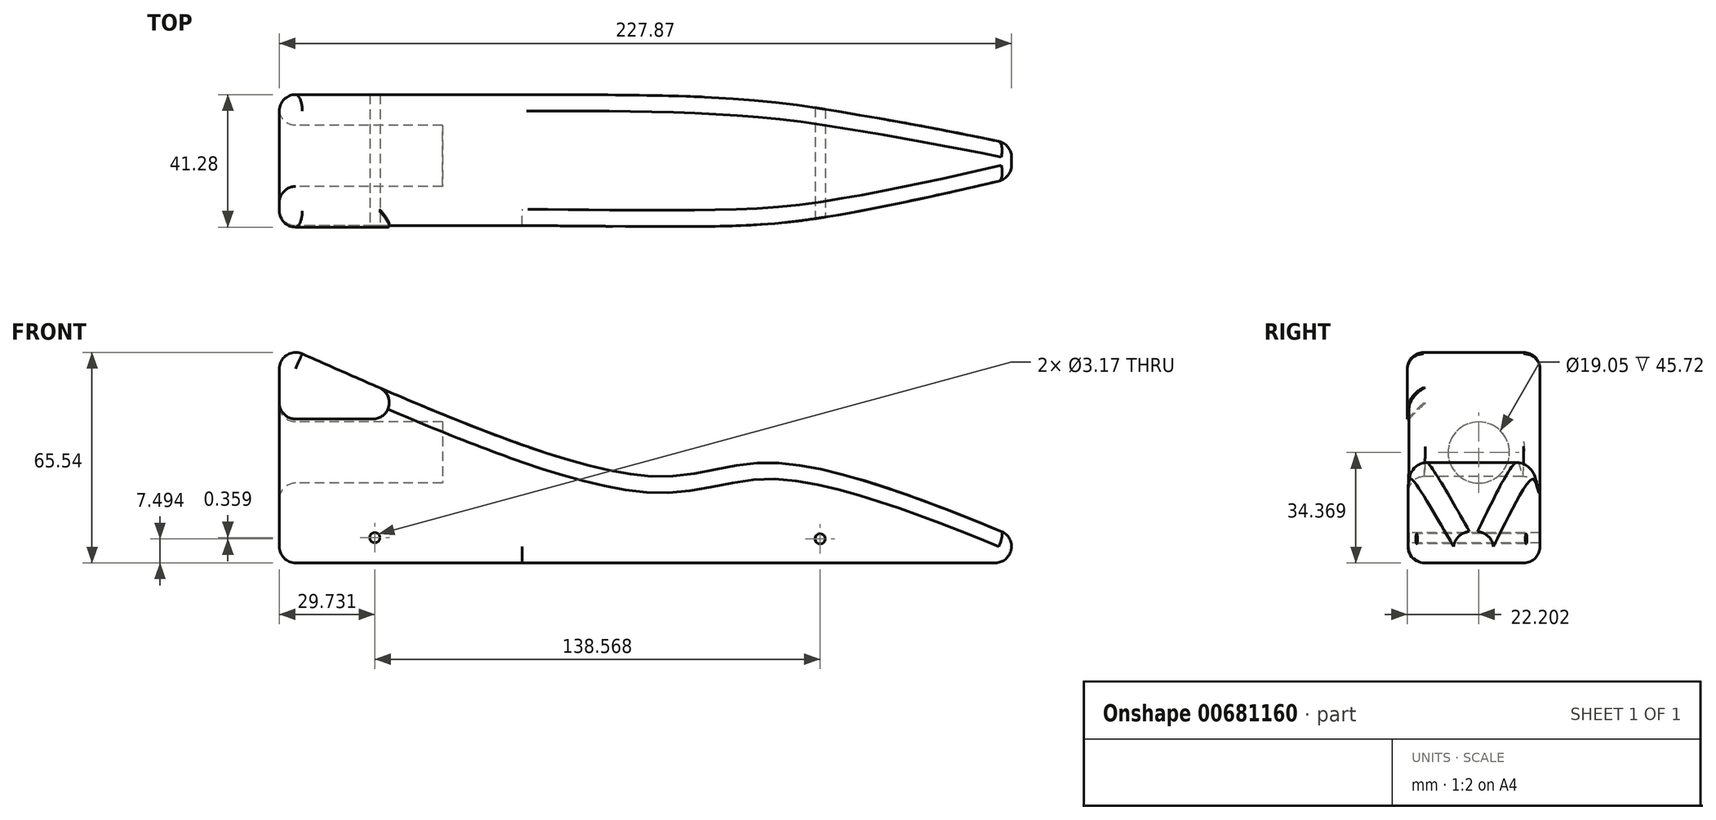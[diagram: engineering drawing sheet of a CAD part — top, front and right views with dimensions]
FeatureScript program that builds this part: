
annotation { "Feature Type Name" : "Feature", "Feature Type Description" : "" }
export const myFeature = defineFeature(function(context is Context, id is Id, definition is map)
    precondition{}
    {
        {
            var Q0;
            Q0=qCreatedBy(makeId("Front.planeOp"),FACE);
            var sketch = newSketch(context, id + "F0", { "sketchPlane" : qUnion([Q0])});
            skLineSegment(sketch, "E0", {"start": v(-84.03, 23.47) * mm, "end": v(-84.03, -44.8) * mm});
            skLineSegment(sketch, "E1", {"start": v(-84.03, -44.8) * mm, "end": v(220.77, -44.8) * mm});
            skLineSegment(sketch, "E2", {"start": v(220.77, -44.8) * mm, "end": v(220.77, -25.76) * mm});
            skLineSegment(sketch, "E3", {"start": v(220.77, -25.76) * mm, "end": v(-84.03, 23.47) * mm});
            skSolve(sketch);
        }
        {
            var Q0;
            Q0 = qSketchRegion(id + "F0", true);
            extrude(context, id + "F1", {"entities" : qUnion([Q0]), "depth" : 41.27 * mm, "offsetDistance" : 25.4 * mm});
        }
        {
            var Q0;
            Q0=makeQuery(id+"F1.opExtrude","SWEPT_FACE",FACE,{"disambiguationData":[OSD([sQuery(id+"F0.wireOp",EDGE,"E0")])]});
            var sketch = newSketch(context, id + "F2", { "sketchPlane" : qUnion([Q0])});
            skCircle(sketch, "E4", {"center": v(19.08, -10.44) * mm, "radius": 9.53 * mm});
            skSolve(sketch);
        }
        {
            var Q0;
            Q0 = qSketchRegion(id + "F2", true);
            extrude(context, id + "F3", {"entities" : qUnion([Q0]), "operationType" : NewBodyOperationType.REMOVE, "oppositeDirection" : true, "depth" : 50.8 * mm, "offsetDistance" : 25.4 * mm});
        }
        {
            var Q0;
            Q0=makeQuery(id+"F1.opExtrude","CAP_FACE",FACE,{"disambiguationData":[OSD([sQuery(id+"F0.wireOp",EDGE,"E0"),sQuery(id+"F0.wireOp",EDGE,"E1"),sQuery(id+"F0.wireOp",EDGE,"E2"),sQuery(id+"F0.wireOp",EDGE,"E3")])],"isStart":false});
            var sketch = newSketch(context, id + "F4", { "sketchPlane" : qUnion([Q0])});
            skFitSpline(sketch, "E5", {"points": [v(-84.03, 23.47) * mm, v(32.93, -17.9) * mm, v(69, -13.59) * mm, v(164, -44.8) * mm], "startDerivative": vector(332.46, -147.88) * mm, "endDerivative": vector(295.83, -125.26) * mm});
            skLineSegment(sketch, "E6", {"start": v(164, -44.8) * mm, "end": v(-84.03, -44.8) * mm});
            skLineSegment(sketch, "E7", {"start": v(-84.03, -44.8) * mm, "end": v(-84.03, 23.47) * mm});
            skSolve(sketch);
        }
        {
            var Q0;
            {var subQ0=sQuery(id+"F4.wireOp",EDGE,"E5");Q0=makeQuery(id+"F4.imprint","IMPRINT",FACE,{"disambiguationData":[TD([[makeQuery(id+"F4.imprint","IMPRINT",EDGE,{"derivedFrom":subQ0}),1.0]])]});}
            extrude(context, id + "F5", {"entities" : qUnion([Q0]), "operationType" : NewBodyOperationType.REMOVE, "oppositeDirection" : true, "depth" : 77.72 * mm, "offsetDistance" : 25.4 * mm});
        }
        {
            var Q0;
            Q0=qCreatedBy(makeId("Top.planeOp"),FACE);
            var sketch = newSketch(context, id + "F6", { "sketchPlane" : qUnion([Q0])});
            skLineSegment(sketch, "E8", {"start": v(-83.84, 0) * mm, "end": v(-8.66, 0) * mm});
            skFitSpline(sketch, "E9", {"points": [v(-8.66, 0) * mm, v(92.78, -5.72) * mm, v(164, -20.64) * mm], "startDerivative": vector(339.58, 0) * mm, "endDerivative": vector(77.36, -27.39) * mm});
            skFitSpline(sketch, "E10", {"points": [v(-8.4, -40.77) * mm, v(92.78, -36.97) * mm, v(164, -20.64) * mm], "startDerivative": vector(348.62, -2.82) * mm, "endDerivative": vector(80.76, 24.97) * mm});
            skLineSegment(sketch, "E11", {"start": v(-8.4, -40.77) * mm, "end": v(-84.86, -40.77) * mm});
            skLineSegment(sketch, "E12", {"start": v(-84.86, -40.77) * mm, "end": v(-83.84, 0) * mm});
            skLineSegment(sketch, "E13.0.0", {"start": v(-84.03, 0) * mm, "end": v(-84.03, -41.28) * mm});
            skFitSpline(sketch, "E13.0.1", {"points": [v(-84.03, -41.28) * mm, v(-38.6, -41.28) * mm, v(31.43, -41.28) * mm, v(69.52, -41.28) * mm, v(127.7, -41.28) * mm, v(164, -41.28) * mm]});
            skLineSegment(sketch, "E13.0.2", {"start": v(164, -41.27) * mm, "end": v(164, 0) * mm});
            skFitSpline(sketch, "E13.0.3", {"points": [v(164, 0) * mm, v(127.7, 0) * mm, v(69.52, 0) * mm, v(31.43, 0) * mm, v(-38.6, 0) * mm, v(-84.03, 0) * mm]});
            skSolve(sketch);
        }
        {
            var Q0;
            {var subQ0=sQuery(id+"F6.wireOp",EDGE,"E9");Q0=makeQuery(id+"F6.imprint","IMPRINT",FACE,{"disambiguationData":[TD([[makeQuery(id+"F6.imprint","IMPRINT",EDGE,{"derivedFrom":subQ0}),1.0]])]});}
            var Q1;
            {var subQ4=sQuery(id+"F6.wireOp",EDGE,"E10");Q1=makeQuery(id+"F6.imprint","IMPRINT",FACE,{"disambiguationData":[TD([[makeQuery(id+"F6.imprint","IMPRINT",EDGE,{"derivedFrom":subQ4}),-1.0]])]});}
            extrude(context, id + "F7", {"entities" : qUnion([Q0, Q1]), "operationType" : NewBodyOperationType.REMOVE, "oppositeDirection" : true, "depth" : 53.6 * mm, "offsetDistance" : 25.4 * mm});
        }
        {
            var Q0;
            Q0=makeQuery(id+"F5.boolean.opBoolean","COPY",FACE,{"derivedFrom":makeQuery(id+"F5.opExtrude","SWEPT_FACE",FACE,{"disambiguationData":[OSD([sQuery(id+"F4.wireOp",EDGE,"E5")])]})});
            fillet(context, id + "F8", {"entities" : qUnion([Q0]), "radius" : 5.08 * mm, "tangentPropagation" : true, "allowEdgeOverflow" : false});
        }
        {
            var Q0;
            Q0=makeQuery(id+"F1.opExtrude","SWEPT_FACE",FACE,{"disambiguationData":[OSD([sQuery(id+"F0.wireOp",EDGE,"E0")])]});
            fillet(context, id + "F9", {"entities" : qUnion([Q0]), "radius" : 5.08 * mm, "tangentPropagation" : true, "allowEdgeOverflow" : false});
        }
        {
            var Q0;
            Q0=makeQuery(id+"F1.opExtrude","SWEPT_FACE",FACE,{"disambiguationData":[OSD([sQuery(id+"F0.wireOp",EDGE,"E1")])]});
            fillet(context, id + "F10", {"entities" : qUnion([Q0]), "radius" : 5.08 * mm, "tangentPropagation" : true, "allowEdgeOverflow" : false});
        }
        {
            var Q0;
            Q0=makeQuery(id+"F7.boolean.opBoolean","COPY",FACE,{"derivedFrom":makeQuery(id+"F7.opExtrude","SWEPT_FACE",FACE,{"disambiguationData":[OSD([sQuery(id+"F6.wireOp",EDGE,"E11")])]})});
            var sketch = newSketch(context, id + "F11", { "sketchPlane" : qUnion([Q0])});
            skCircle(sketch, "E14", {"center": v(-54.3, -36.96) * mm, "radius": 1.59 * mm});
            skCircle(sketch, "E15", {"center": v(84.27, -37.32) * mm, "radius": 1.59 * mm});
            skSolve(sketch);
        }
        {
            var Q0;
            Q0 = qSketchRegion(id + "F11", true);
            extrude(context, id + "F12", {"entities" : qUnion([Q0]), "operationType" : NewBodyOperationType.REMOVE, "oppositeDirection" : true, "depth" : 76.2 * mm, "offsetDistance" : 25.4 * mm});
        }
    });
